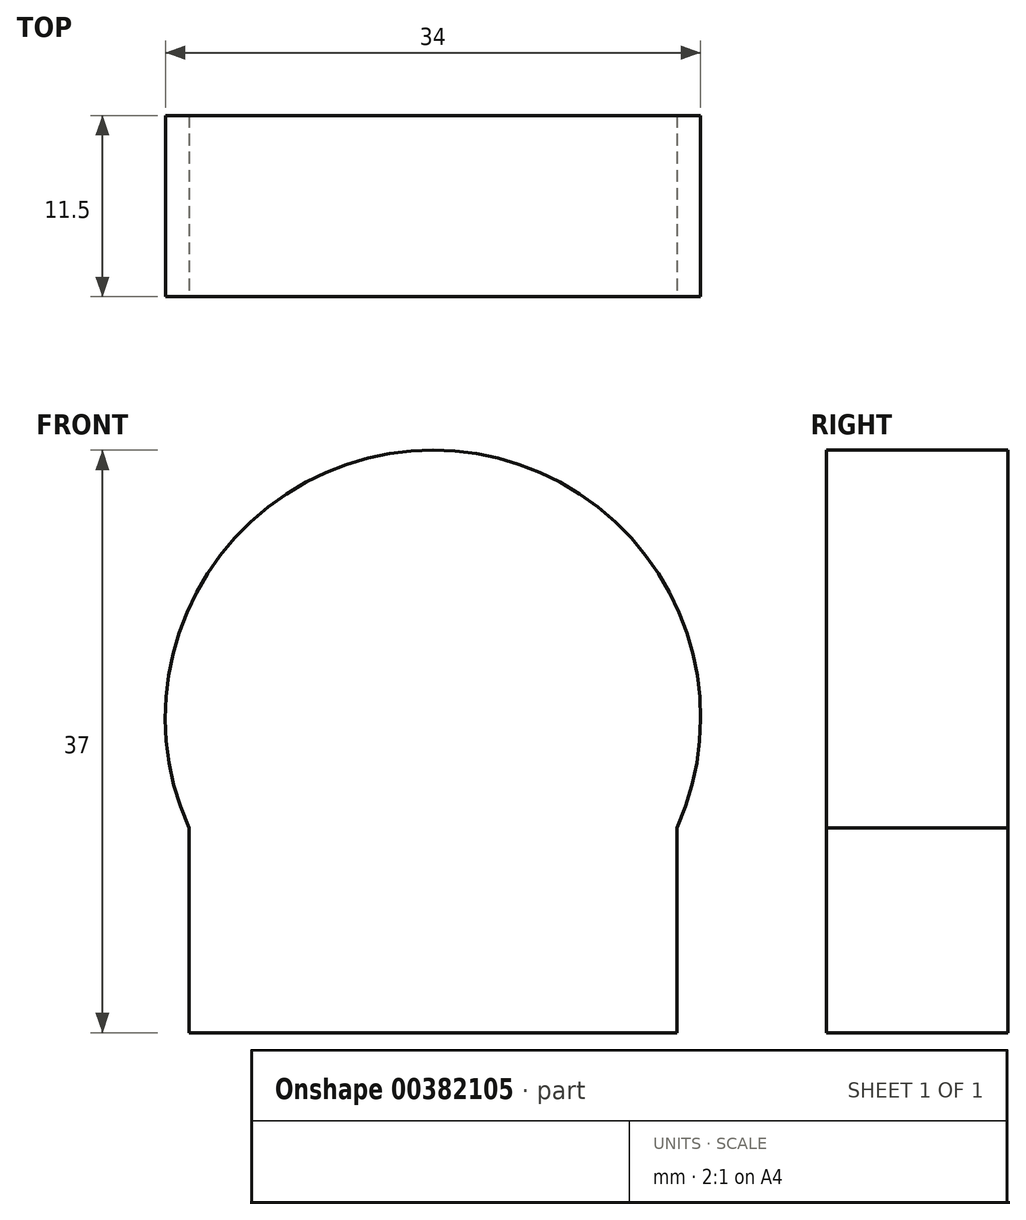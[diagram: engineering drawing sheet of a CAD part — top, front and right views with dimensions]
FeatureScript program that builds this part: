
annotation { "Feature Type Name" : "Feature", "Feature Type Description" : "" }
export const myFeature = defineFeature(function(context is Context, id is Id, definition is map)
    precondition{}
    {
        {
            var Q0;
            Q0=qCreatedBy(makeId("Front.planeOp"),FACE);
            var sketch = newSketch(context, id + "F0", { "sketchPlane" : qUnion([Q0])});
            skCircle(sketch, "E0", {"center": v(0, 0) * mm, "radius": 17 * mm});
            skLineSegment(sketch, "E1", {"start": v(-15.5, -20) * mm, "end": v(0, -20) * mm});
            skLineSegment(sketch, "E2", {"start": v(0, 0) * mm, "end": v(0, -20) * mm, "construction": true});
            skLineSegment(sketch, "E3", {"start": v(-15.5, -20) * mm, "end": v(-15.5, -6.98) * mm});
            skLineSegment(sketch, "E4.MirrorCS", {"start": v(15.5, -20) * mm, "end": v(0, -20) * mm});
            skLineSegment(sketch, "E5.MirrorCS", {"start": v(15.5, -20) * mm, "end": v(15.5, -6.98) * mm});
            skSolve(sketch);
        }
        {
            var Q0;
            {var subQ0=sQuery(id+"F0.wireOp",EDGE,"E0");var subQ1=makeQuery(id+"F0.imprint","INTERSECT",VERTEX,{"derivedFrom":[subQ0,sQuery(id+"F0.wireOp",EDGE,"E3")]});Q0=makeQuery(id+"F0.imprint","IMPRINT",FACE,{"disambiguationData":[TD([[makeQuery(id+"F0.imprint","IMPRINT",EDGE,{"disambiguationData":[TD([[subQ1,-1.0]])],"derivedFrom":subQ0}),1.0]])]});}
            var Q1;
            Q1=makeQuery(id+"F0.imprint","IMPRINT",FACE,{"disambiguationData":[TD([[makeQuery(id+"F0.imprint","IMPRINT",EDGE,{"derivedFrom":sQuery(id+"F0.wireOp",EDGE,"E1")}),1.0]])]});
            extrude(context, id + "F1", {"entities" : qUnion([Q0, Q1]), "oppositeDirection" : true, "depth" : 11.5 * mm});
        }
    });
